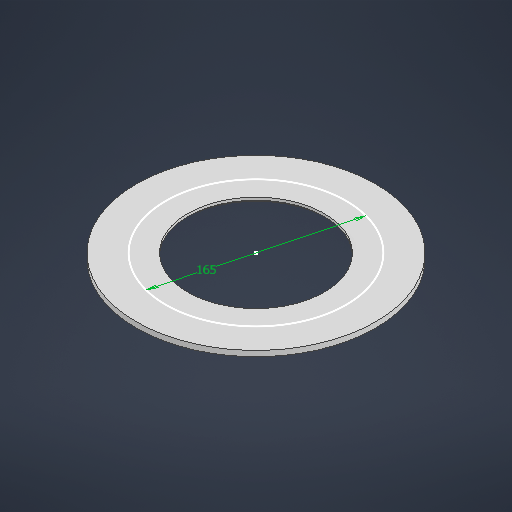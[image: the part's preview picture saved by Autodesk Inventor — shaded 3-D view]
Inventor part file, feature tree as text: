
AUTODESK INVENTOR PART (.ipt)
format: ipt  version: 2025 (Build 290162000, 162)  size: 214,528 bytes
history: native  units: in
note: dims shown in document units (in); Inventor stores cm internally (conversion verified against a paired STEP export)
features: sketch x3, extrude x3
ambient origin geometry x8: Origin, YZ Plane, XZ Plane, XY Plane, X Axis, Y Axis, Z Axis, Center Point
bodies: Solid1 (feature_tree)
feature tree (6):
  sketch  "Sketch1"  dims[d0=8.622in d1=4.9213in]
  extrude  "Extrusion1"  Depth=4.9213in
  extrude  "Extrusion2"  Depth=0.1969in TaperAngle=0.0deg
  extrude  "Extrusion3"  Depth=0.0197in
  sketch  "Sketch3"  dims[d5=0.1004in d6=0.0in d7=5.9055in d8=5.9843in d9=0.0197in d10=0.0in d11=6.4961in]
  sketch  "Sketch2"  dims[d2=5.1181in d3=0.1969in d4=0.0in]
